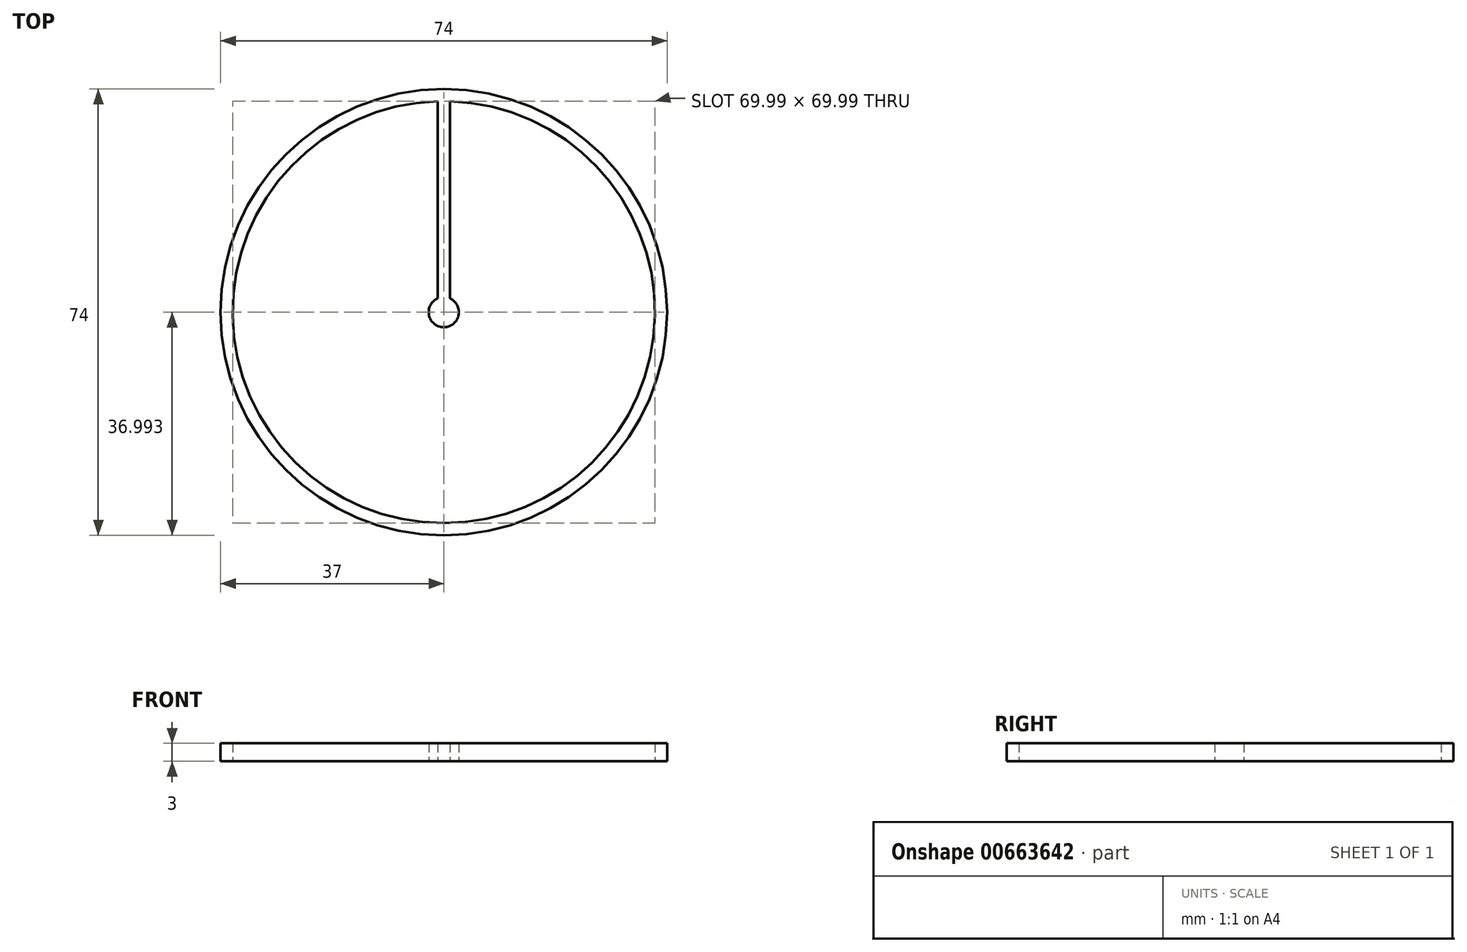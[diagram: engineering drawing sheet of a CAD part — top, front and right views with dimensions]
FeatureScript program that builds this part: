
annotation { "Feature Type Name" : "Feature", "Feature Type Description" : "" }
export const myFeature = defineFeature(function(context is Context, id is Id, definition is map)
    precondition{}
    {
        {
            var Q0;
            Q0=qCreatedBy(makeId("Top.planeOp"),FACE);
            var sketch = newSketch(context, id + "F0", { "sketchPlane" : qUnion([Q0])});
            skCircle(sketch, "E0", {"center": v(0, 0) * mm, "radius": 2.5 * mm});
            skCircle(sketch, "E1", {"center": v(0, 0) * mm, "radius": 35 * mm});
            skCircle(sketch, "E2", {"center": v(0, 0) * mm, "radius": 37 * mm});
            skLineSegment(sketch, "E3", {"start": v(0, 35) * mm, "end": v(0, 1.21) * mm, "construction": true});
            skLineSegment(sketch, "E4.bottom", {"start": v(-1, 0.59) * mm, "end": v(1, 0.59) * mm});
            skLineSegment(sketch, "E4.top", {"start": v(-1, 35.63) * mm, "end": v(1, 35.63) * mm});
            skLineSegment(sketch, "E4.left", {"start": v(-1, 0.59) * mm, "end": v(-1, 35.63) * mm});
            skLineSegment(sketch, "E4.right", {"start": v(1, 0.59) * mm, "end": v(1, 35.63) * mm});
            skPoint(sketch, "E4.middle", {"position": v(0, 18.1) * mm});
            skSolve(sketch);
        }
        {
            var Q0;
            Q0=makeQuery(id+"F0.imprint","IMPRINT",FACE,{"disambiguationData":[TD([[makeQuery(id+"F0.imprint","IMPRINT",EDGE,{"derivedFrom":sQuery(id+"F0.wireOp",EDGE,"E2")}),1.0]])]});
            var Q1;
            {var subQ5=sQuery(id+"F0.wireOp",EDGE,"E4.bottom");Q1=makeQuery(id+"F0.imprint","IMPRINT",FACE,{"disambiguationData":[TD([[makeQuery(id+"F0.imprint","IMPRINT",EDGE,{"derivedFrom":subQ5}),-1.0]])]});}
            var Q2;
            {var subQ5=sQuery(id+"F0.wireOp",EDGE,"E4.bottom");Q2=makeQuery(id+"F0.imprint","IMPRINT",FACE,{"disambiguationData":[TD([[makeQuery(id+"F0.imprint","IMPRINT",EDGE,{"derivedFrom":subQ5}),1.0]])]});}
            var Q3;
            {var subQ5=sQuery(id+"F0.wireOp",EDGE,"E4.top");Q3=makeQuery(id+"F0.imprint","IMPRINT",FACE,{"disambiguationData":[TD([[makeQuery(id+"F0.imprint","IMPRINT",EDGE,{"derivedFrom":subQ5}),-1.0]])]});}
            extrude(context, id + "F1", {"entities" : qUnion([Q0, Q1, Q2, Q3]), "depth" : 3 * mm, "offsetDistance" : 25 * mm});
        }
        {
            var Q0;
            {var subQ5=sQuery(id+"F0.wireOp",EDGE,"E4.bottom");Q0=makeQuery(id+"F0.imprint","IMPRINT",FACE,{"disambiguationData":[TD([[makeQuery(id+"F0.imprint","IMPRINT",EDGE,{"derivedFrom":subQ5}),1.0]])]});}
            var Q1;
            {var subQ0=sQuery(id+"F0.wireOp",EDGE,"E4.left");var subQ1=sQuery(id+"F0.wireOp",EDGE,"E0");var subQ2=makeQuery(id+"F0.imprint","INTERSECT",VERTEX,{"derivedFrom":[subQ1,subQ0]});Q1=makeQuery(id+"F0.imprint","IMPRINT",FACE,{"disambiguationData":[TD([[makeQuery(id+"F0.imprint","IMPRINT",EDGE,{"disambiguationData":[TD([[subQ2,1.0]])],"derivedFrom":subQ1}),-1.0]])]});}
            var Q2;
            {var subQ5=sQuery(id+"F0.wireOp",EDGE,"E4.top");Q2=makeQuery(id+"F0.imprint","IMPRINT",FACE,{"disambiguationData":[TD([[makeQuery(id+"F0.imprint","IMPRINT",EDGE,{"derivedFrom":subQ5}),-1.0]])]});}
            extrude(context, id + "F2", {"entities" : qUnion([Q0, Q1, Q2]), "operationType" : NewBodyOperationType.ADD, "depth" : 3 * mm, "offsetDistance" : 25 * mm});
        }
    });
